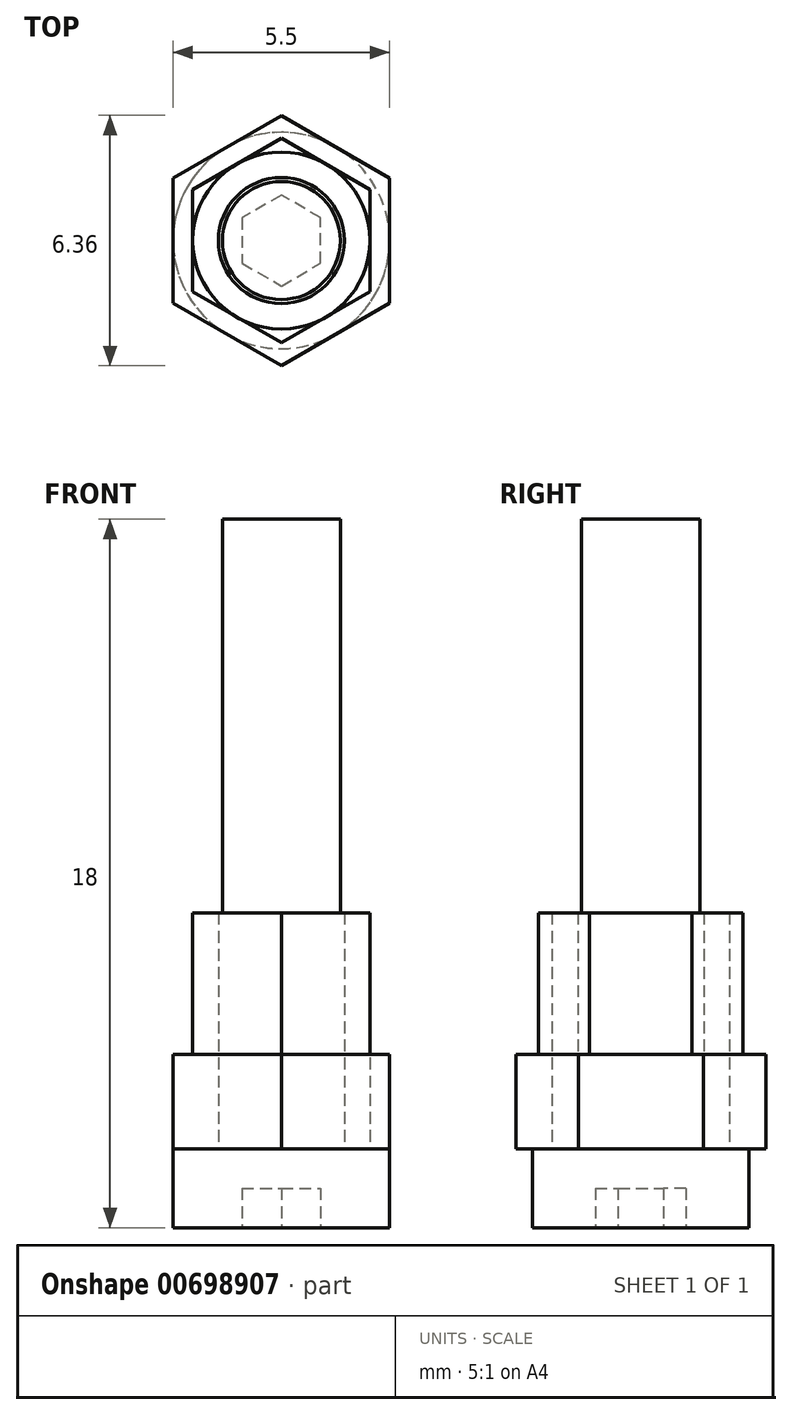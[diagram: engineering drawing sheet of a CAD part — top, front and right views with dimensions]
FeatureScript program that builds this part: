
annotation { "Feature Type Name" : "Feature", "Feature Type Description" : "" }
export const myFeature = defineFeature(function(context is Context, id is Id, definition is map)
    precondition{}
    {
        {
            var Q0;
            Q0=qCreatedBy(makeId("Top.planeOp"),FACE);
            var sketch = newSketch(context, id + "F0", { "sketchPlane" : qUnion([Q0])});
            skCircle(sketch, "E0", {"center": v(0, 0) * mm, "radius": 2 * mm});
            skCircle(sketch, "E1", {"center": v(0, 0) * mm, "radius": 1 * mm});
            skSolve(sketch);
        }
        {
            var Q0;
            Q0=makeQuery(id+"F0.imprint","IMPRINT",FACE,{"disambiguationData":[TD([[makeQuery(id+"F0.imprint","IMPRINT",EDGE,{"derivedFrom":sQuery(id+"F0.wireOp",EDGE,"E0")}),1.0]])]});
            var Q1;
            Q1=makeQuery(id+"F0.imprint","IMPRINT",FACE,{"disambiguationData":[TD([[makeQuery(id+"F0.imprint","IMPRINT",EDGE,{"derivedFrom":sQuery(id+"F0.wireOp",EDGE,"E1")}),1.0]])]});
            extrude(context, id + "F1", {"entities" : qUnion([Q0, Q1]), "oppositeDirection" : true, "depth" : 1.75 * mm});
        }
        {
            var Q0;
            Q0=makeQuery(id+"F0.imprint","IMPRINT",FACE,{"disambiguationData":[TD([[makeQuery(id+"F0.imprint","IMPRINT",EDGE,{"derivedFrom":sQuery(id+"F0.wireOp",EDGE,"E1")}),1.0]])]});
            extrude(context, id + "F2", {"entities" : qUnion([Q0]), "operationType" : NewBodyOperationType.ADD, "depth" : 10.5 * mm});
        }
        {
            var Q0;
            Q0=makeQuery(id+"F1.opExtrude","CAP_FACE",FACE,{"disambiguationData":[OSD([sQuery(id+"F0.wireOp",EDGE,"E0")])],"isStart":false});
            var sketch = newSketch(context, id + "F3", { "sketchPlane" : qUnion([Q0])});
            skLineSegment(sketch, "E2.bottom", {"start": v(1.25, 0.25) * mm, "end": v(-1.25, 0.25) * mm});
            skLineSegment(sketch, "E2.top", {"start": v(1.25, -0.25) * mm, "end": v(-1.25, -0.25) * mm});
            skLineSegment(sketch, "E2.left", {"start": v(1.25, 0.25) * mm, "end": v(1.25, -0.25) * mm});
            skLineSegment(sketch, "E2.right", {"start": v(-1.25, 0.25) * mm, "end": v(-1.25, -0.25) * mm});
            skPoint(sketch, "E2.middle", {"position": v(0, 0) * mm});
            skLineSegment(sketch, "E3.bottom", {"start": v(0.25, 1.25) * mm, "end": v(-0.25, 1.25) * mm});
            skLineSegment(sketch, "E3.top", {"start": v(0.25, -1.25) * mm, "end": v(-0.25, -1.25) * mm});
            skLineSegment(sketch, "E3.left", {"start": v(0.25, 1.25) * mm, "end": v(0.25, -1.25) * mm});
            skLineSegment(sketch, "E3.right", {"start": v(-0.25, 1.25) * mm, "end": v(-0.25, -1.25) * mm});
            skSolve(sketch);
        }
        {
            var Q0;
            {var subQ5=sQuery(id+"F3.wireOp",EDGE,"E3.bottom");Q0=makeQuery(id+"F3.imprint","IMPRINT",FACE,{"disambiguationData":[TD([[makeQuery(id+"F3.imprint","IMPRINT",EDGE,{"derivedFrom":subQ5}),1.0]])]});}
            var Q1;
            {var subQ0=sQuery(id+"F3.wireOp",EDGE,"E3.left");var subQ1=sQuery(id+"F3.wireOp",EDGE,"E2.bottom");var subQ2=makeQuery(id+"F3.imprint","INTERSECT",VERTEX,{"derivedFrom":[subQ1,subQ0]});Q1=makeQuery(id+"F3.imprint","IMPRINT",FACE,{"disambiguationData":[TD([[makeQuery(id+"F3.imprint","IMPRINT",EDGE,{"disambiguationData":[TD([[subQ2,-1.0]])],"derivedFrom":subQ1}),1.0]])]});}
            var Q2;
            {var subQ0=sQuery(id+"F3.wireOp",EDGE,"E2.left");Q2=makeQuery(id+"F3.imprint","IMPRINT",FACE,{"disambiguationData":[TD([[makeQuery(id+"F3.imprint","IMPRINT",EDGE,{"derivedFrom":subQ0}),-1.0]])]});}
            var Q3;
            {var subQ5=sQuery(id+"F3.wireOp",EDGE,"E3.top");Q3=makeQuery(id+"F3.imprint","IMPRINT",FACE,{"disambiguationData":[TD([[makeQuery(id+"F3.imprint","IMPRINT",EDGE,{"derivedFrom":subQ5}),-1.0]])]});}
            var Q4;
            {var subQ0=sQuery(id+"F3.wireOp",EDGE,"E2.right");Q4=makeQuery(id+"F3.imprint","IMPRINT",FACE,{"disambiguationData":[TD([[makeQuery(id+"F3.imprint","IMPRINT",EDGE,{"derivedFrom":subQ0}),1.0]])]});}
            extrude(context, id + "F4", {"entities" : qUnion([Q0, Q1, Q2, Q3, Q4]), "operationType" : NewBodyOperationType.REMOVE, "oppositeDirection" : true, "depth" : 0.5 * mm});
        }
        {
            var Q0;
            Q0=qCreatedBy(makeId("Top.planeOp"),FACE);
            var sketch = newSketch(context, id + "F5", { "sketchPlane" : qUnion([Q0])});
            skCircle(sketch, "E4.cCircle", {"center": v(0, 0) * mm, "radius": 2 * mm, "construction": true});
            skLineSegment(sketch, "E4.0", {"start": v(2, 1.15) * mm, "end": v(2, -1.15) * mm});
            skLineSegment(sketch, "E4.1", {"start": v(2, -1.15) * mm, "end": v(0, -2.3) * mm});
            skLineSegment(sketch, "E4.2", {"start": v(0, -2.3) * mm, "end": v(-2, -1.15) * mm});
            skLineSegment(sketch, "E4.3", {"start": v(-2, -1.15) * mm, "end": v(-2, 1.15) * mm});
            skLineSegment(sketch, "E4.4", {"start": v(-2, 1.15) * mm, "end": v(0, 2.3) * mm});
            skLineSegment(sketch, "E4.5", {"start": v(0, 2.3) * mm, "end": v(2, 1.15) * mm});
            skPoint(sketch, "E4.0.midPoint", {"position": v(2, 0) * mm});
            skCircle(sketch, "E5", {"center": v(0, 0) * mm, "radius": 1.1 * mm});
            skSolve(sketch);
        }
        {
            var Q0;
            Q0=makeQuery(id+"F5.imprint","IMPRINT",FACE,{"disambiguationData":[TD([[makeQuery(id+"F5.imprint","IMPRINT",EDGE,{"derivedFrom":sQuery(id+"F5.wireOp",EDGE,"E4.0")}),-1.0]])]});
            extrude(context, id + "F6", {"entities" : qUnion([Q0]), "depth" : 1.6 * mm});
        }
        {
            var Q0;
            Q0=makeQuery(id+"F1.opExtrude","CAP_EDGE",EDGE,{"disambiguationData":[OSD([sQuery(id+"F0.wireOp",EDGE,"E0")])],"isStart":false});
            fillet(context, id + "F7", {"entities" : qUnion([Q0]), "radius" : 0.5 * mm, "tangentPropagation" : true, "allowEdgeOverflow" : false});
        }
        {
            var Q0;
            Q0=qCreatedBy(makeId("Top.planeOp"),FACE);
            var sketch = newSketch(context, id + "F8", { "sketchPlane" : qUnion([Q0])});
            skCircle(sketch, "E6.cCircle", {"center": v(0, 0) * mm, "radius": 2.25 * mm, "construction": true});
            skLineSegment(sketch, "E6.0", {"start": v(2.25, 1.3) * mm, "end": v(2.25, -1.3) * mm});
            skLineSegment(sketch, "E6.1", {"start": v(2.25, -1.3) * mm, "end": v(0, -2.6) * mm});
            skLineSegment(sketch, "E6.2", {"start": v(0, -2.6) * mm, "end": v(-2.25, -1.3) * mm});
            skLineSegment(sketch, "E6.3", {"start": v(-2.25, -1.3) * mm, "end": v(-2.25, 1.3) * mm});
            skLineSegment(sketch, "E6.4", {"start": v(-2.25, 1.3) * mm, "end": v(0, 2.6) * mm});
            skLineSegment(sketch, "E6.5", {"start": v(0, 2.6) * mm, "end": v(2.25, 1.3) * mm});
            skPoint(sketch, "E6.0.midPoint", {"position": v(2.25, 0) * mm});
            skCircle(sketch, "E7", {"center": v(0, 0) * mm, "radius": 1.5 * mm});
            skSolve(sketch);
        }
        {
            var Q0;
            Q0=makeQuery(id+"F8.imprint","IMPRINT",FACE,{"disambiguationData":[TD([[makeQuery(id+"F8.imprint","IMPRINT",EDGE,{"derivedFrom":sQuery(id+"F8.wireOp",EDGE,"E6.0")}),-1.0]])]});
            var Q1;
            Q1=makeQuery(id+"F8.imprint","IMPRINT",FACE,{"disambiguationData":[TD([[makeQuery(id+"F8.imprint","IMPRINT",EDGE,{"derivedFrom":sQuery(id+"F8.wireOp",EDGE,"E7")}),1.0]])]});
            extrude(context, id + "F9", {"entities" : qUnion([Q0, Q1]), "depth" : 6 * mm});
        }
        {
            var Q0;
            Q0=makeQuery(id+"F8.imprint","IMPRINT",FACE,{"disambiguationData":[TD([[makeQuery(id+"F8.imprint","IMPRINT",EDGE,{"derivedFrom":sQuery(id+"F8.wireOp",EDGE,"E7")}),1.0]])]});
            extrude(context, id + "F10", {"entities" : qUnion([Q0]), "operationType" : NewBodyOperationType.REMOVE, "depth" : 2.8 * mm});
        }
        {
            var Q0;
            Q0=makeQuery(id+"F9.opExtrude","CAP_FACE",FACE,{"disambiguationData":[OSD([sQuery(id+"F8.wireOp",EDGE,"E6.0"),sQuery(id+"F8.wireOp",EDGE,"E6.1"),sQuery(id+"F8.wireOp",EDGE,"E6.2"),sQuery(id+"F8.wireOp",EDGE,"E6.3"),sQuery(id+"F8.wireOp",EDGE,"E6.4"),sQuery(id+"F8.wireOp",EDGE,"E6.5")])],"isStart":false});
            var sketch = newSketch(context, id + "F11", { "sketchPlane" : qUnion([Q0])});
            skCircle(sketch, "E8", {"center": v(0, 0) * mm, "radius": 1.5 * mm});
            skSolve(sketch);
        }
        {
            var Q0;
            Q0=makeQuery(id+"F11.imprint","IMPRINT",FACE,{"disambiguationData":[TD([[makeQuery(id+"F11.imprint","IMPRINT",EDGE,{"derivedFrom":sQuery(id+"F11.wireOp",EDGE,"E8")}),1.0]])]});
            extrude(context, id + "F12", {"entities" : qUnion([Q0]), "operationType" : NewBodyOperationType.ADD, "depth" : 4.7 * mm});
        }
        {
            var Q0;
            Q0=qCreatedBy(makeId("Top.planeOp"),FACE);
            var sketch = newSketch(context, id + "F13", { "sketchPlane" : qUnion([Q0])});
            skCircle(sketch, "E9.cCircle", {"center": v(0, 0) * mm, "radius": 2.75 * mm, "construction": true});
            skLineSegment(sketch, "E9.0", {"start": v(2.75, 1.59) * mm, "end": v(2.75, -1.59) * mm});
            skLineSegment(sketch, "E9.1", {"start": v(2.75, -1.59) * mm, "end": v(0, -3.18) * mm});
            skLineSegment(sketch, "E9.2", {"start": v(0, -3.18) * mm, "end": v(-2.75, -1.59) * mm});
            skLineSegment(sketch, "E9.3", {"start": v(-2.75, -1.59) * mm, "end": v(-2.75, 1.59) * mm});
            skLineSegment(sketch, "E9.4", {"start": v(-2.75, 1.59) * mm, "end": v(0, 3.18) * mm});
            skLineSegment(sketch, "E9.5", {"start": v(0, 3.18) * mm, "end": v(2.75, 1.59) * mm});
            skPoint(sketch, "E9.0.midPoint", {"position": v(2.75, 0) * mm});
            skCircle(sketch, "E10", {"center": v(0, 0) * mm, "radius": 1.5 * mm});
            skSolve(sketch);
        }
        {
            var Q0;
            Q0=makeQuery(id+"F13.imprint","IMPRINT",FACE,{"disambiguationData":[TD([[makeQuery(id+"F13.imprint","IMPRINT",EDGE,{"derivedFrom":sQuery(id+"F13.wireOp",EDGE,"E9.0")}),-1.0]])]});
            extrude(context, id + "F14", {"entities" : qUnion([Q0]), "depth" : 2.4 * mm});
        }
        {
            var Q0;
            Q0=qCreatedBy(makeId("Top.planeOp"),FACE);
            var sketch = newSketch(context, id + "F15", { "sketchPlane" : qUnion([Q0])});
            skCircle(sketch, "E11", {"center": v(0, 0) * mm, "radius": 2.25 * mm});
            skCircle(sketch, "E12", {"center": v(0, 0) * mm, "radius": 1.6 * mm});
            skSolve(sketch);
        }
        {
            var Q0;
            Q0=makeQuery(id+"F15.imprint","IMPRINT",FACE,{"disambiguationData":[TD([[makeQuery(id+"F15.imprint","IMPRINT",EDGE,{"derivedFrom":sQuery(id+"F15.wireOp",EDGE,"E11")}),1.0]])]});
            extrude(context, id + "F16", {"entities" : qUnion([Q0]), "depth" : 6 * mm});
        }
        {
            var Q0;
            Q0=qCreatedBy(makeId("Top.planeOp"),FACE);
            var sketch = newSketch(context, id + "F17", { "sketchPlane" : qUnion([Q0])});
            skCircle(sketch, "E13", {"center": v(0, 0) * mm, "radius": 2.75 * mm});
            skCircle(sketch, "E14", {"center": v(0, 0) * mm, "radius": 1.5 * mm});
            skSolve(sketch);
        }
        {
            var Q0;
            Q0=makeQuery(id+"F17.imprint","IMPRINT",FACE,{"disambiguationData":[TD([[makeQuery(id+"F17.imprint","IMPRINT",EDGE,{"derivedFrom":sQuery(id+"F17.wireOp",EDGE,"E13")}),1.0]])]});
            var Q1;
            Q1=makeQuery(id+"F17.imprint","IMPRINT",FACE,{"disambiguationData":[TD([[makeQuery(id+"F17.imprint","IMPRINT",EDGE,{"derivedFrom":sQuery(id+"F17.wireOp",EDGE,"E14")}),1.0]])]});
            extrude(context, id + "F18", {"entities" : qUnion([Q0, Q1]), "oppositeDirection" : true, "depth" : 2 * mm});
        }
        {
            var Q0;
            Q0=makeQuery(id+"F17.imprint","IMPRINT",FACE,{"disambiguationData":[TD([[makeQuery(id+"F17.imprint","IMPRINT",EDGE,{"derivedFrom":sQuery(id+"F17.wireOp",EDGE,"E14")}),1.0]])]});
            extrude(context, id + "F19", {"entities" : qUnion([Q0]), "operationType" : NewBodyOperationType.ADD, "depth" : 16 * mm});
        }
        {
            var Q0;
            Q0=makeQuery(id+"F18.opExtrude","CAP_FACE",FACE,{"disambiguationData":[OSD([sQuery(id+"F17.wireOp",EDGE,"E13")])],"isStart":false});
            var sketch = newSketch(context, id + "F20", { "sketchPlane" : qUnion([Q0])});
            skCircle(sketch, "E15.cCircle", {"center": v(0, 0) * mm, "radius": 1 * mm, "construction": true});
            skLineSegment(sketch, "E15.0", {"start": v(1, 0.58) * mm, "end": v(1, -0.58) * mm});
            skLineSegment(sketch, "E15.1", {"start": v(1, -0.58) * mm, "end": v(0, -1.15) * mm});
            skLineSegment(sketch, "E15.2", {"start": v(0, -1.15) * mm, "end": v(-1, -0.58) * mm});
            skLineSegment(sketch, "E15.3", {"start": v(-1, -0.58) * mm, "end": v(-1, 0.58) * mm});
            skLineSegment(sketch, "E15.4", {"start": v(-1, 0.58) * mm, "end": v(0, 1.15) * mm});
            skLineSegment(sketch, "E15.5", {"start": v(0, 1.15) * mm, "end": v(1, 0.58) * mm});
            skPoint(sketch, "E15.0.midPoint", {"position": v(1, 0) * mm});
            skSolve(sketch);
        }
        {
            var Q0;
            Q0=makeQuery(id+"F20.imprint","IMPRINT",FACE,{"disambiguationData":[TD([[makeQuery(id+"F20.imprint","IMPRINT",EDGE,{"derivedFrom":sQuery(id+"F20.wireOp",EDGE,"E15.0")}),-1.0]])]});
            extrude(context, id + "F21", {"entities" : qUnion([Q0]), "operationType" : NewBodyOperationType.REMOVE, "oppositeDirection" : true, "depth" : 1 * mm});
        }
    });
